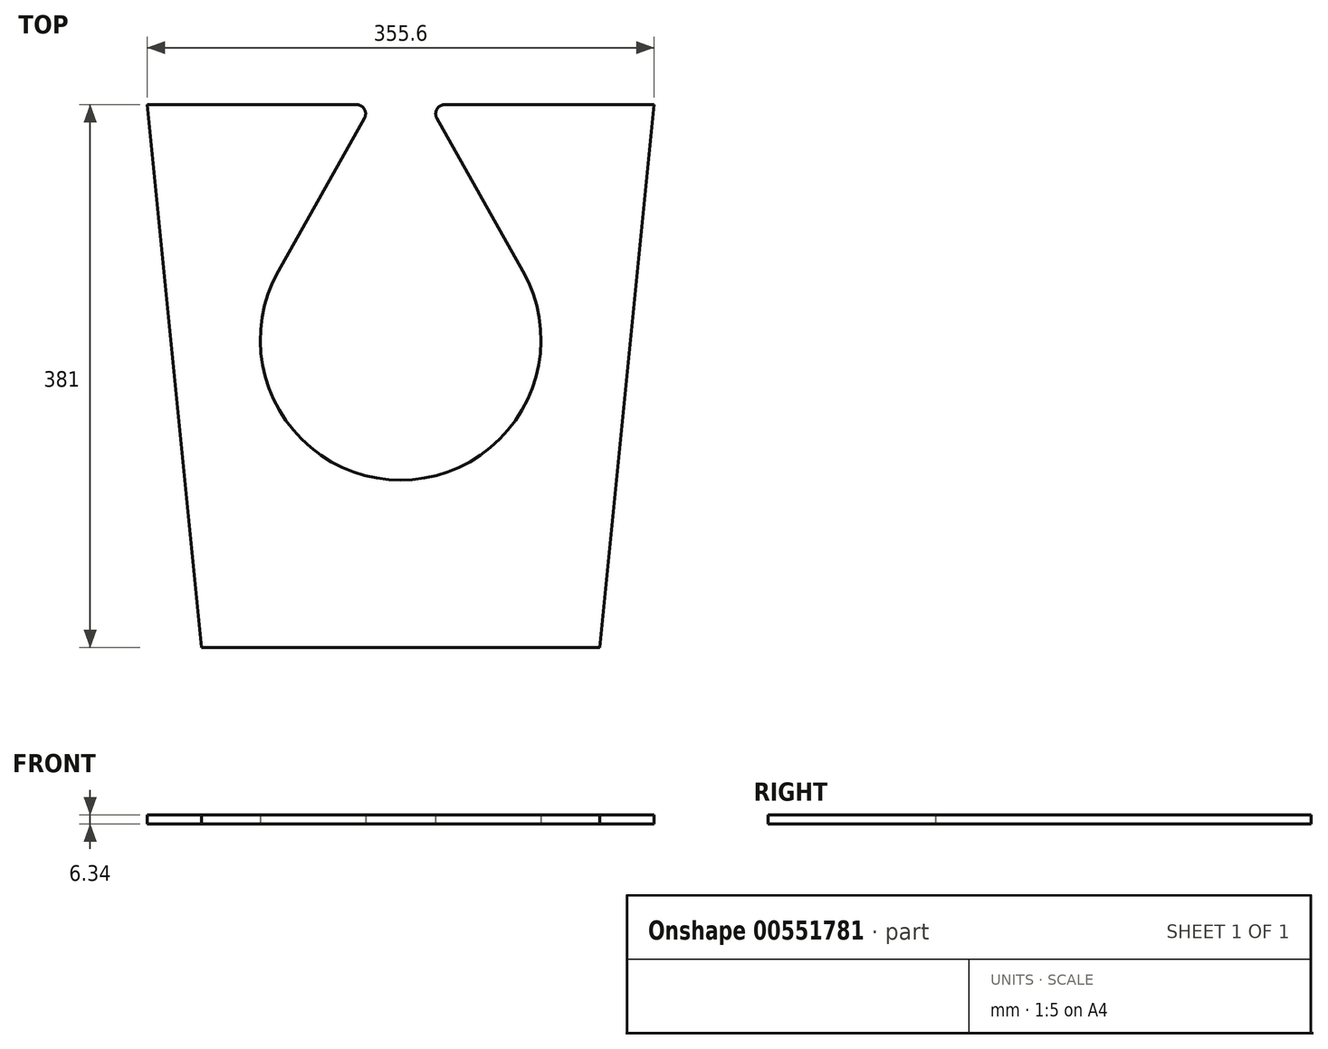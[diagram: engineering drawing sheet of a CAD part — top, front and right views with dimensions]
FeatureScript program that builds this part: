
annotation { "Feature Type Name" : "Feature", "Feature Type Description" : "" }
export const myFeature = defineFeature(function(context is Context, id is Id, definition is map)
    precondition{}
    {
        {
            var Q0;
            Q0=qCreatedBy(makeId("Top.planeOp"),FACE);
            var sketch = newSketch(context, id + "F0", { "sketchPlane" : qUnion([Q0])});
            skLineSegment(sketch, "E0", {"start": v(0, 0) * mm, "end": v(-139.7, 0) * mm});
            skLineSegment(sketch, "E1", {"start": v(0, 0) * mm, "end": v(139.7, 0) * mm});
            skLineSegment(sketch, "E2", {"start": v(0, 0) * mm, "end": v(0, 381) * mm, "construction": true});
            skLineSegment(sketch, "E3", {"start": v(-30.93, 381) * mm, "end": v(-177.8, 381) * mm});
            skLineSegment(sketch, "E4", {"start": v(30.93, 381) * mm, "end": v(177.8, 381) * mm});
            skLineSegment(sketch, "E5", {"start": v(-177.8, 381) * mm, "end": v(-139.7, 0) * mm});
            skLineSegment(sketch, "E6", {"start": v(177.8, 381) * mm, "end": v(139.7, 0) * mm});
            skPoint(sketch, "E7", {"position": v(0, 215.9) * mm});
            skCircle(sketch, "E8", {"center": v(0, 215.9) * mm, "radius": 98.43 * mm});
            skLineSegment(sketch, "E9", {"start": v(0, 381) * mm, "end": v(-12.7, 381) * mm, "construction": true});
            skLineSegment(sketch, "E10", {"start": v(0, 381) * mm, "end": v(12.7, 381) * mm, "construction": true});
            skLineSegment(sketch, "E11", {"start": v(-25.4, 371.54) * mm, "end": v(-85.8, 264.14) * mm});
            skLineSegment(sketch, "E12", {"start": v(25.4, 371.54) * mm, "end": v(85.8, 264.14) * mm});
            skPoint(sketch, "E13.newPointA", {"position": v(0, 381) * mm});
            skArc(sketch, "E13.filletArc", {"start": v(-25.4, 371.54) * mm, "mid": v(-25.45, 377.86) * mm, "end": v(-30.93, 381) * mm});
            skArc(sketch, "E14.filletArc", {"start": v(30.93, 381) * mm, "mid": v(25.45, 377.86) * mm, "end": v(25.4, 371.54) * mm});
            skSolve(sketch);
        }
        {
            var Q0;
            Q0=makeQuery(id+"F0.imprint","IMPRINT",FACE,{"disambiguationData":[TD([[makeQuery(id+"F0.imprint","IMPRINT",EDGE,{"derivedFrom":sQuery(id+"F0.wireOp",EDGE,"E0")}),-1.0]])]});
            extrude(context, id + "F1", {"entities" : qUnion([Q0]), "endBound" : BoundingType.SYMMETRIC, "depth" : 6.35 * mm, "offsetDistance" : 25.4 * mm});
        }
    });
